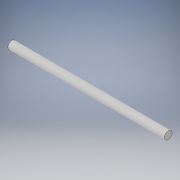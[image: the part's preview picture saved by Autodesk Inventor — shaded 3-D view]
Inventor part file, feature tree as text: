
AUTODESK INVENTOR PART (.ipt)
format: ipt  version: 2018 (Build 220112000, 112)  size: 89,600 bytes
history: native  units: in
note: dims shown in document units (in); Inventor stores cm internally (conversion verified against a paired STEP export)
features: extrude x1, sketch x1
ambient origin geometry x8: Origin, YZ Plane, XZ Plane, XY Plane, X Axis, Y Axis, Z Axis, Center Point
bodies: Solid1 (feature_tree)
feature tree (2):
  extrude  "Extrusion1"  Depth=2.0in TaperAngle=0.0deg
  sketch  "Sketch1"  dims[d0=0.0984in d1=2.0in d2=0.0in]
